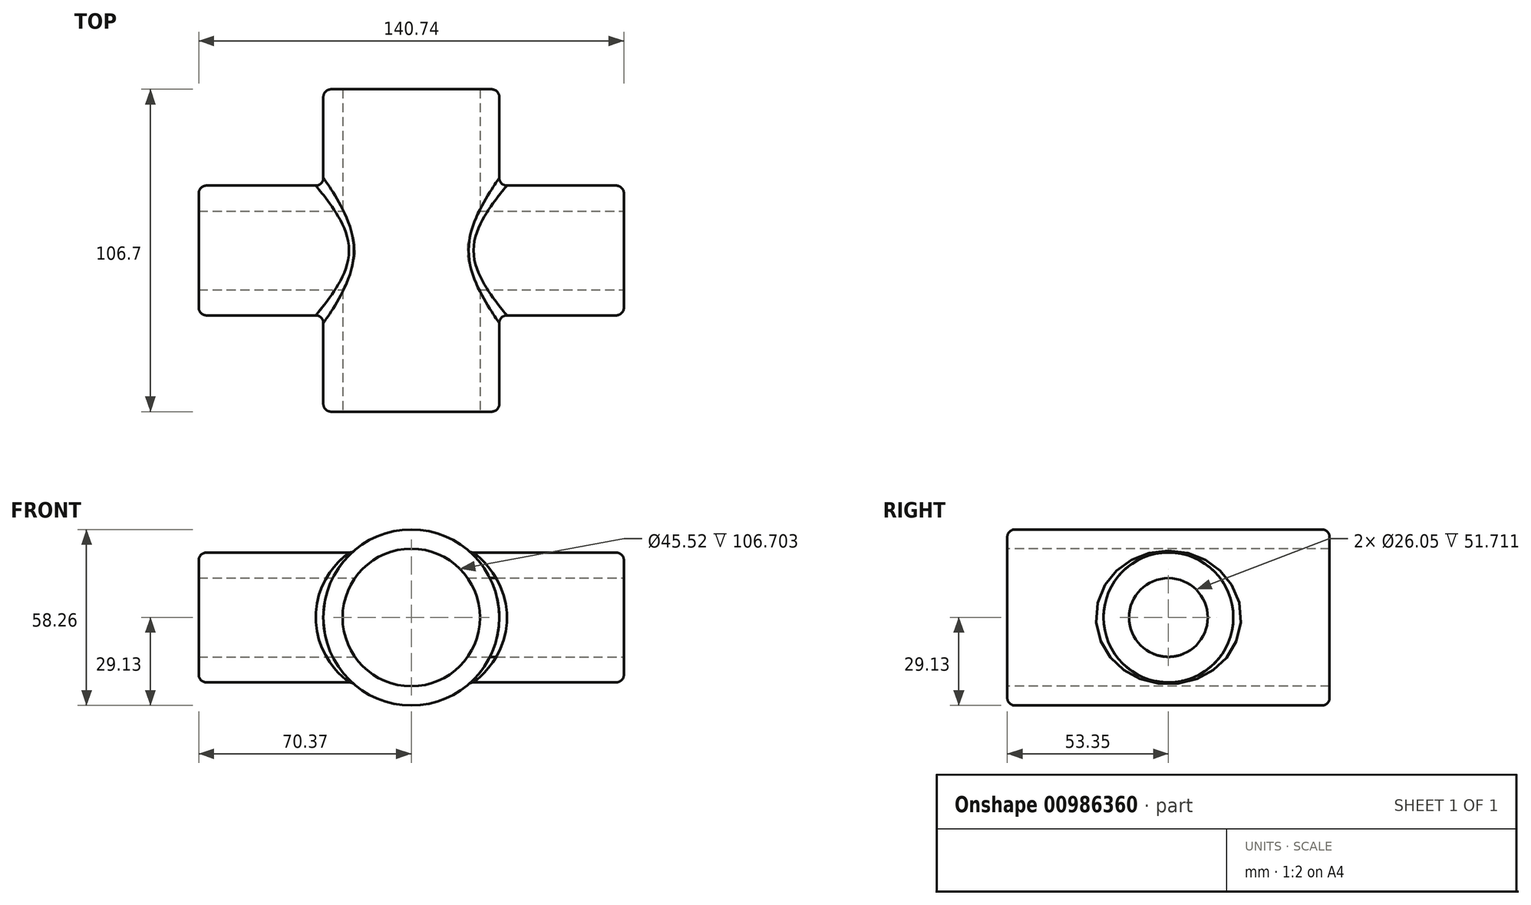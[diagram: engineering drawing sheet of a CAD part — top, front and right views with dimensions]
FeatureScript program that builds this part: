
annotation { "Feature Type Name" : "Feature", "Feature Type Description" : "" }
export const myFeature = defineFeature(function(context is Context, id is Id, definition is map)
    precondition{}
    {
        {
            var Q0;
            Q0=qCreatedBy(makeId("Front.planeOp"),FACE);
            var sketch = newSketch(context, id + "F0", { "sketchPlane" : qUnion([Q0])});
            skCircle(sketch, "E0", {"center": v(0, 0) * mm, "radius": 29.13 * mm});
            skSolve(sketch);
        }
        {
            var Q0;
            Q0 = qSketchRegion(id + "F0", true);
            extrude(context, id + "F1", {"entities" : qUnion([Q0]), "endBound" : BoundingType.SYMMETRIC, "depth" : 106.7 * mm, "offsetDistance" : 25.4 * mm});
        }
        {
            var Q0;
            Q0=qCreatedBy(makeId("Right.planeOp"),FACE);
            var sketch = newSketch(context, id + "F2", { "sketchPlane" : qUnion([Q0])});
            skCircle(sketch, "E1", {"center": v(0, 0) * mm, "radius": 21.48 * mm});
            skSolve(sketch);
        }
        {
            var Q0;
            Q0 = qSketchRegion(id + "F2", true);
            extrude(context, id + "F3", {"entities" : qUnion([Q0]), "operationType" : NewBodyOperationType.ADD, "endBound" : BoundingType.SYMMETRIC, "depth" : 140.74 * mm, "hasOffset" : true, "offsetDistance" : 25.4 * mm});
        }
        {
            var Q0;
            {var subQ0=sQuery(id+"F2.wireOp",EDGE,"E1");Q0=makeQuery(id+"F3.boolean.opBoolean","SPLIT",FACE,{"disambiguationData":[TD([makeQuery(id+"F3.opExtrude","CAP_FACE",FACE,{"disambiguationData":[OSD([subQ0])],"isStart":true})])],"derivedFrom":makeQuery(id+"F3.opExtrude","SWEPT_FACE",FACE,{"disambiguationData":[OSD([subQ0])]})});}
            var Q1;
            Q1=makeQuery(id+"F3.boolean.opBoolean","INTERSECT",EDGE,{"disambiguationData":[OD(1.0)],"derivedFrom":[makeQuery(id+"F1.opExtrude","SWEPT_FACE",FACE,{"disambiguationData":[OSD([sQuery(id+"F0.wireOp",EDGE,"E0")])]}),makeQuery(id+"F3.opExtrude","SWEPT_FACE",FACE,{"disambiguationData":[OSD([sQuery(id+"F2.wireOp",EDGE,"E1")])]})]});
            var Q2;
            Q2=makeQuery(id+"F1.opExtrude","CAP_EDGE",EDGE,{"disambiguationData":[OSD([sQuery(id+"F0.wireOp",EDGE,"E0")])],"isStart":false});
            var Q3;
            Q3=makeQuery(id+"F1.opExtrude","CAP_EDGE",EDGE,{"disambiguationData":[OSD([sQuery(id+"F0.wireOp",EDGE,"E0")])],"isStart":true});
            var Q4;
            Q4=makeQuery(id+"F3.opExtrude","CAP_EDGE",EDGE,{"disambiguationData":[OSD([sQuery(id+"F2.wireOp",EDGE,"E1")])],"isStart":false});
            fillet(context, id + "F4", {"entities" : qUnion([Q0, Q1, Q2, Q3, Q4]), "radius" : 2.54 * mm, "tangentPropagation" : true, "allowEdgeOverflow" : false});
        }
        {
            var Q0;
            Q0=qCreatedBy(makeId("Front.planeOp"),FACE);
            var sketch = newSketch(context, id + "F5", { "sketchPlane" : qUnion([Q0])});
            skCircle(sketch, "E2", {"center": v(0, 0) * mm, "radius": 11.7 * mm});
            skCircle(sketch, "E3", {"center": v(0, 0) * mm, "radius": 22.76 * mm});
            skSolve(sketch);
        }
        {
            var Q0;
            Q0 = qSketchRegion(id + "F5", true);
            extrude(context, id + "F6", {"entities" : qUnion([Q0]), "operationType" : NewBodyOperationType.REMOVE, "endBound" : BoundingType.SYMMETRIC, "oppositeDirection" : true, "depth" : 145.47 * mm, "offsetDistance" : 25.4 * mm});
        }
        {
            var Q0;
            Q0=qCreatedBy(makeId("Front.planeOp"),FACE);
            var sketch = newSketch(context, id + "F7", { "sketchPlane" : qUnion([Q0])});
            skCircle(sketch, "E4", {"center": v(0, 0) * mm, "radius": 17 * mm});
            skSolve(sketch);
        }
        {
            var Q0;
            Q0 = qSketchRegion(id + "F7", true);
            extrude(context, id + "F8", {"entities" : qUnion([Q0]), "operationType" : NewBodyOperationType.REMOVE, "endBound" : BoundingType.SYMMETRIC, "oppositeDirection" : true, "depth" : 132.27 * mm, "offsetDistance" : 25.4 * mm});
        }
        {
            var Q0;
            Q0=qCreatedBy(makeId("Right.planeOp"),FACE);
            var sketch = newSketch(context, id + "F9", { "sketchPlane" : qUnion([Q0])});
            skCircle(sketch, "E5", {"center": v(0, 0) * mm, "radius": 13.03 * mm});
            skSolve(sketch);
        }
        {
            var Q0;
            Q0 = qSketchRegion(id + "F9", true);
            extrude(context, id + "F10", {"entities" : qUnion([Q0]), "operationType" : NewBodyOperationType.REMOVE, "endBound" : BoundingType.SYMMETRIC, "oppositeDirection" : true, "depth" : 178.76 * mm, "offsetDistance" : 25.4 * mm});
        }
    });
